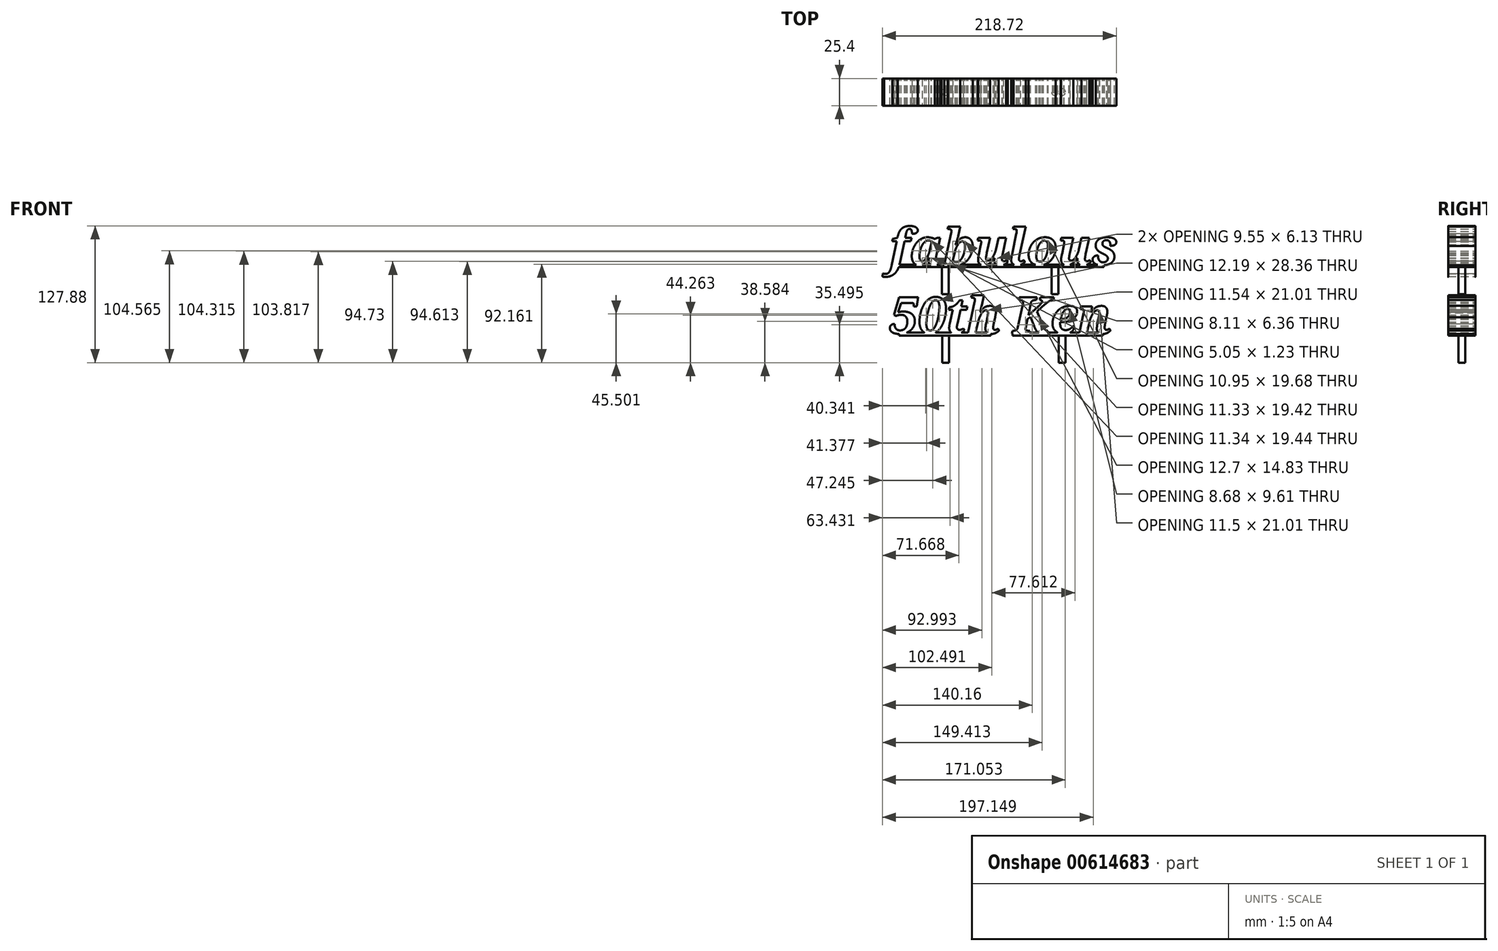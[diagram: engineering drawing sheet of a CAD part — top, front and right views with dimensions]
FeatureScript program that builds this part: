
annotation { "Feature Type Name" : "Feature", "Feature Type Description" : "" }
export const myFeature = defineFeature(function(context is Context, id is Id, definition is map)
    precondition{}
    {
        {
            var Q0;
            Q0=qCreatedBy(makeId("Front.planeOp"),FACE);
            var sketch = newSketch(context, id + "F0", { "sketchPlane" : qUnion([Q0])});
            skText(sketch, "E0", { "text": "fabulous \n50th Ken", "fontName": "NotoSerif-BoldItalic.ttf"});
            skLineSegment(sketch, "E1.bottom", {"start": v(-107.52, 22.07) * mm, "end": v(86.92, 22.07) * mm});
            skLineSegment(sketch, "E1.top", {"start": v(-107.52, 19.84) * mm, "end": v(86.92, 19.84) * mm});
            skLineSegment(sketch, "E1.left", {"start": v(-107.52, 22.07) * mm, "end": v(-107.52, 19.84) * mm});
            skLineSegment(sketch, "E1.right", {"start": v(86.92, 22.07) * mm, "end": v(86.92, 19.84) * mm});
            skLineSegment(sketch, "E2.bottom", {"start": v(-104.4, -41.4) * mm, "end": v(-18.73, -41.4) * mm});
            skLineSegment(sketch, "E2.top", {"start": v(-104.4, -44.08) * mm, "end": v(-18.73, -44.08) * mm});
            skLineSegment(sketch, "E2.left", {"start": v(-104.4, -41.4) * mm, "end": v(-104.4, -44.08) * mm});
            skLineSegment(sketch, "E2.right", {"start": v(-18.73, -41.4) * mm, "end": v(-18.73, -44.08) * mm});
            skLineSegment(sketch, "E3.bottom", {"start": v(1.7, -41.4) * mm, "end": v(85.95, -41.4) * mm});
            skLineSegment(sketch, "E3.top", {"start": v(1.7, -44.1) * mm, "end": v(85.95, -44.1) * mm});
            skLineSegment(sketch, "E3.left", {"start": v(1.7, -41.4) * mm, "end": v(1.7, -44.1) * mm});
            skLineSegment(sketch, "E3.right", {"start": v(85.95, -41.4) * mm, "end": v(85.95, -44.1) * mm});
            const initialGuessF0  = {"E0": [-0.1136, 0.02207, 1, 0, 0.03397]};
            skSetInitialGuess(sketch, initialGuessF0);
            skSolve(sketch);
        }
        {
            var Q0;
            Q0 = qSketchRegion(id + "F0", true);
            extrude(context, id + "F1", {"entities" : qUnion([Q0]), "depth" : 25.4 * mm, "offsetDistance" : 25.4 * mm});
        }
        {
            var Q0;
            Q0=makeQuery(id+"F1.opExtrude","SWEPT_FACE",FACE,{"disambiguationData":[OSD([sQuery(id+"F0.wireOp",EDGE,"E2.top")])]});
            var sketch = newSketch(context, id + "F2", { "sketchPlane" : qUnion([Q0])});
            skLineSegment(sketch, "E4", {"start": v(-99.54, 12.7) * mm, "end": v(82.41, 12.7) * mm, "construction": true});
            skCircle(sketch, "E5", {"center": v(-61.01, 12.7) * mm, "radius": 3.18 * mm});
            skCircle(sketch, "E6", {"center": v(47.87, 12.7) * mm, "radius": 3.18 * mm});
            skSolve(sketch);
        }
        {
            var Q0;
            Q0 = qSketchRegion(id + "F2", true);
            extrude(context, id + "F3", {"entities" : qUnion([Q0]), "depth" : 25.4 * mm, "offsetDistance" : 25.4 * mm});
        }
        {
            var Q0;
            Q0=makeQuery(id+"F1.opExtrude","SWEPT_FACE",FACE,{"disambiguationData":[OSD([sQuery(id+"F0.wireOp",EDGE,"E1.top")])]});
            var sketch = newSketch(context, id + "F4", { "sketchPlane" : qUnion([Q0])});
            skLineSegment(sketch, "E7", {"start": v(-61.33, 12.7) * mm, "end": v(120.63, 12.7) * mm, "construction": true});
            skCircle(sketch, "E8", {"center": v(-61.33, 12.7) * mm, "radius": 3.18 * mm});
            skCircle(sketch, "E9", {"center": v(41.08, 12.7) * mm, "radius": 3.18 * mm});
            skSolve(sketch);
        }
        {
            var Q0;
            Q0 = qSketchRegion(id + "F4", true);
            extrude(context, id + "F5", {"entities" : qUnion([Q0]), "operationType" : NewBodyOperationType.ADD, "depth" : 25.4 * mm, "offsetDistance" : 25.4 * mm});
        }
    });
